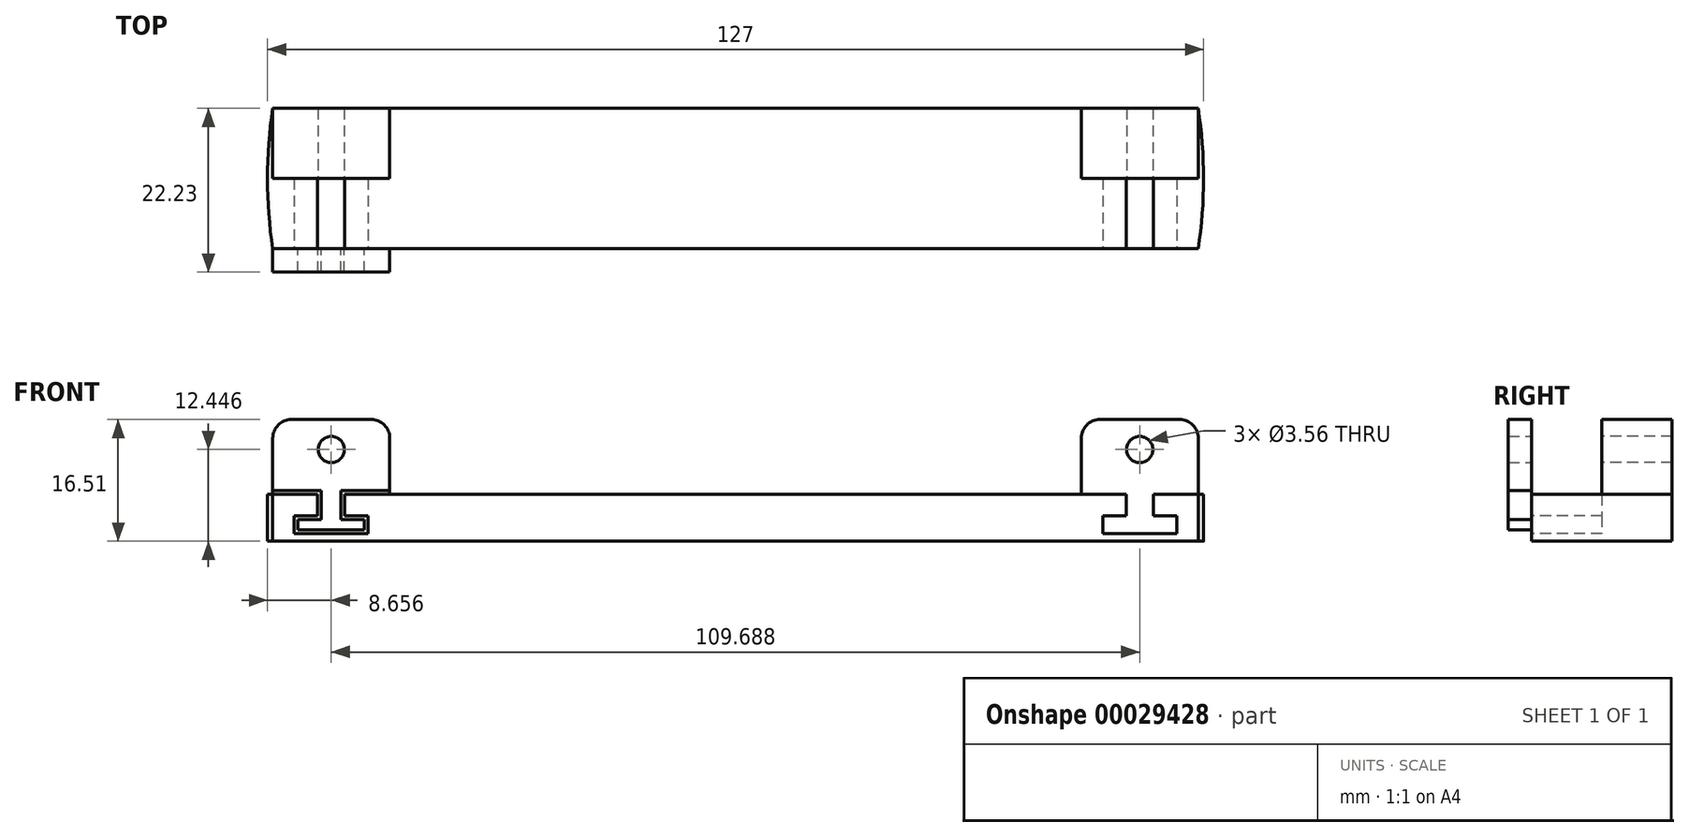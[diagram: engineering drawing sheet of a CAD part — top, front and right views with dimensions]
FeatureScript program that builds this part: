
annotation { "Feature Type Name" : "Feature", "Feature Type Description" : "" }
export const myFeature = defineFeature(function(context is Context, id is Id, definition is map)
    precondition{}
    {
        {
            var Q0;
            Q0=qCreatedBy(makeId("Top.planeOp"),FACE);
            var sketch = newSketch(context, id + "F0", { "sketchPlane" : qUnion([Q0])});
            skArc(sketch, "E0", {"start": v(-62.78, 9.52) * mm, "mid": v(-63.5, 0) * mm, "end": v(-62.78, -9.53) * mm});
            skLineSegment(sketch, "E1", {"start": v(0, 9.53) * mm, "end": v(-62.78, 9.53) * mm});
            skLineSegment(sketch, "E2", {"start": v(0, 9.53) * mm, "end": v(62.78, 9.53) * mm});
            skLineSegment(sketch, "E3", {"start": v(0, -9.53) * mm, "end": v(62.78, -9.53) * mm});
            skLineSegment(sketch, "E4", {"start": v(0, -9.53) * mm, "end": v(-62.78, -9.53) * mm});
            skArc(sketch, "E5.trimOffspring", {"start": v(62.78, -9.52) * mm, "mid": v(63.5, 0) * mm, "end": v(62.78, 9.53) * mm});
            skSolve(sketch);
        }
        {
            var Q0;
            Q0 = qSketchRegion(id + "F0", true);
            extrude(context, id + "F1", {"entities" : qUnion([Q0]), "depth" : 6.35 * mm});
        }
        {
            var Q0;
            Q0=makeQuery(id+"F1.opExtrude","SWEPT_FACE",FACE,{"disambiguationData":[OSD([sQuery(id+"F0.wireOp",EDGE,"E3"),sQuery(id+"F0.wireOp",EDGE,"E4")])]});
            var sketch = newSketch(context, id + "F2", { "sketchPlane" : qUnion([Q0])});
            skLineSegment(sketch, "E6", {"start": v(0, 0) * mm, "end": v(0, 18.8) * mm});
            skLineSegment(sketch, "E7", {"start": v(-56.69, 6.35) * mm, "end": v(-56.69, 3.43) * mm});
            skLineSegment(sketch, "E8", {"start": v(-56.69, 3.43) * mm, "end": v(-59.86, 3.43) * mm});
            skLineSegment(sketch, "E9", {"start": v(-59.86, 3.43) * mm, "end": v(-59.86, 1.02) * mm});
            skLineSegment(sketch, "E10", {"start": v(-59.86, 1.02) * mm, "end": v(-49.83, 1.02) * mm});
            skLineSegment(sketch, "E11", {"start": v(-49.83, 1.02) * mm, "end": v(-49.83, 3.43) * mm});
            skLineSegment(sketch, "E12", {"start": v(-49.83, 3.43) * mm, "end": v(-53, 3.43) * mm});
            skLineSegment(sketch, "E13", {"start": v(-53, 3.43) * mm, "end": v(-53, 6.35) * mm});
            skLineSegment(sketch, "E14", {"start": v(-56.69, 6.35) * mm, "end": v(-53, 6.35) * mm});
            skLineSegment(sketch, "E15.MirrorCS", {"start": v(53, 3.43) * mm, "end": v(53, 6.35) * mm});
            skLineSegment(sketch, "E16.MirrorCS", {"start": v(56.69, 6.35) * mm, "end": v(53, 6.35) * mm});
            skLineSegment(sketch, "E17.MirrorCS", {"start": v(49.83, 3.43) * mm, "end": v(53, 3.43) * mm});
            skLineSegment(sketch, "E18.MirrorCS", {"start": v(56.69, 6.35) * mm, "end": v(56.69, 3.43) * mm});
            skLineSegment(sketch, "E19.MirrorCS", {"start": v(56.69, 3.43) * mm, "end": v(59.86, 3.43) * mm});
            skLineSegment(sketch, "E20.MirrorCS", {"start": v(59.86, 3.43) * mm, "end": v(59.86, 1.02) * mm});
            skLineSegment(sketch, "E21.MirrorCS", {"start": v(49.83, 1.02) * mm, "end": v(49.83, 3.43) * mm});
            skLineSegment(sketch, "E22.MirrorCS", {"start": v(59.86, 1.02) * mm, "end": v(49.83, 1.02) * mm});
            skSolve(sketch);
        }
        {
            var Q0;
            Q0 = qSketchRegion(id + "F2", true);
            extrude(context, id + "F3", {"entities" : qUnion([Q0]), "operationType" : NewBodyOperationType.REMOVE, "oppositeDirection" : true, "depth" : 25.4 * mm});
        }
        {
            var Q0;
            Q0=qCreatedBy(makeId("Front.planeOp"),FACE);
            var sketch = newSketch(context, id + "F4", { "sketchPlane" : qUnion([Q0])});
            skLineSegment(sketch, "E23.0", {"start": v(-62.78, 6.35) * mm, "end": v(-62.78, 0) * mm});
            skLineSegment(sketch, "E24", {"start": v(-62.78, 6.35) * mm, "end": v(-62.78, 13.97) * mm});
            skLineSegment(sketch, "E25.0", {"start": v(-53, 3.43) * mm, "end": v(-53, 6.35) * mm});
            skLineSegment(sketch, "E26.0", {"start": v(-56.69, 6.35) * mm, "end": v(-56.69, 3.43) * mm});
            skLineSegment(sketch, "E27", {"start": v(-46.9, 13.97) * mm, "end": v(-46.9, 6.35) * mm});
            skLineSegment(sketch, "E28", {"start": v(-46.9, 6.35) * mm, "end": v(-46.9, 0) * mm});
            skLineSegment(sketch, "E29", {"start": v(-46.9, 0) * mm, "end": v(-62.78, 0) * mm});
            skLineSegment(sketch, "E30", {"start": v(-60.24, 16.51) * mm, "end": v(-49.45, 16.51) * mm});
            skPoint(sketch, "E31.visualSharp", {"position": v(-62.78, 16.51) * mm});
            skArc(sketch, "E31.filletArc", {"start": v(-60.24, 16.51) * mm, "mid": v(-62.04, 15.77) * mm, "end": v(-62.78, 13.97) * mm});
            skPoint(sketch, "E32.visualSharp", {"position": v(-46.9, 16.51) * mm});
            skArc(sketch, "E32.filletArc", {"start": v(-46.9, 13.97) * mm, "mid": v(-47.65, 15.77) * mm, "end": v(-49.45, 16.51) * mm});
            skSolve(sketch);
        }
        {
            var Q0;
            Q0 = qSketchRegion(id + "F4", true);
            extrude(context, id + "F5", {"entities" : qUnion([Q0]), "operationType" : NewBodyOperationType.ADD, "oppositeDirection" : true, "depth" : 3.17 * mm});
        }
        {
            var Q0;
            Q0=makeQuery(id+"F5.opExtrude","CAP_FACE",FACE,{"disambiguationData":[OSD([sQuery(id+"F4.wireOp",EDGE,"E23.0"),sQuery(id+"F4.wireOp",EDGE,"E24"),sQuery(id+"F4.wireOp",EDGE,"E27"),sQuery(id+"F4.wireOp",EDGE,"E28"),sQuery(id+"F4.wireOp",EDGE,"E29"),sQuery(id+"F4.wireOp",EDGE,"E30"),sQuery(id+"F4.wireOp",EDGE,"E31.filletArc"),sQuery(id+"F4.wireOp",EDGE,"E32.filletArc")])],"isStart":true});
            var sketch = newSketch(context, id + "F6", { "sketchPlane" : qUnion([Q0])});
            skCircle(sketch, "E33", {"center": v(-54.84, 12.45) * mm, "radius": 1.78 * mm});
            skSolve(sketch);
        }
        {
            var Q0;
            Q0 = qSketchRegion(id + "F6", true);
            extrude(context, id + "F7", {"entities" : qUnion([Q0]), "operationType" : NewBodyOperationType.REMOVE, "oppositeDirection" : true, "depth" : 25.4 * mm});
        }
        {
            var Q0;
            Q0=makeQuery(id+"F1.opExtrude","SWEPT_BODY",BODY,{"disambiguationData":[OSD([sQuery(id+"F0.wireOp",EDGE,"E0"),sQuery(id+"F0.wireOp",EDGE,"E1"),sQuery(id+"F0.wireOp",EDGE,"E2"),sQuery(id+"F0.wireOp",EDGE,"E3"),sQuery(id+"F0.wireOp",EDGE,"E4"),sQuery(id+"F0.wireOp",EDGE,"E5.trimOffspring")])]});
            var Q1;
            Q1=qCreatedBy(makeId("Right.planeOp"),FACE);
            mirror(context, id + "F8", {"operationType" : NewBodyOperationType.ADD, "entities" : qUnion([Q0]), "mirrorPlane" : qUnion([Q1])});
        }
        {
            var Q0;
            Q0=makeQuery(id+"F1.opExtrude","SWEPT_FACE",FACE,{"disambiguationData":[OSD([sQuery(id+"F0.wireOp",EDGE,"E3"),sQuery(id+"F0.wireOp",EDGE,"E4")])]});
            var sketch = newSketch(context, id + "F9", { "sketchPlane" : qUnion([Q0])});
            skLineSegment(sketch, "E34", {"start": v(-56.18, 2.92) * mm, "end": v(-59.35, 2.92) * mm});
            skLineSegment(sketch, "E35", {"start": v(-59.35, 2.92) * mm, "end": v(-59.35, 1.52) * mm});
            skLineSegment(sketch, "E36", {"start": v(-59.35, 1.52) * mm, "end": v(-50.34, 1.52) * mm});
            skLineSegment(sketch, "E37", {"start": v(-50.34, 1.52) * mm, "end": v(-50.34, 2.92) * mm});
            skLineSegment(sketch, "E38", {"start": v(-50.34, 2.92) * mm, "end": v(-53.51, 2.92) * mm});
            skLineSegment(sketch, "E39", {"start": v(-53.51, 2.92) * mm, "end": v(-53.51, 6.86) * mm});
            skLineSegment(sketch, "E40", {"start": v(-56.18, 2.92) * mm, "end": v(-56.18, 6.86) * mm});
            skLineSegment(sketch, "E41.0", {"start": v(-62.78, 6.86) * mm, "end": v(-62.78, 13.97) * mm});
            skArc(sketch, "E42.0", {"start": v(-60.24, 16.51) * mm, "mid": v(-62.04, 15.77) * mm, "end": v(-62.78, 13.97) * mm});
            skLineSegment(sketch, "E43.0", {"start": v(-60.24, 16.51) * mm, "end": v(-49.45, 16.51) * mm});
            skArc(sketch, "E44.0", {"start": v(-46.9, 13.97) * mm, "mid": v(-47.65, 15.77) * mm, "end": v(-49.45, 16.51) * mm});
            skLineSegment(sketch, "E45.0", {"start": v(-46.9, 13.97) * mm, "end": v(-46.9, 6.86) * mm});
            skLineSegment(sketch, "E46", {"start": v(-56.18, 6.86) * mm, "end": v(-62.78, 6.86) * mm});
            skLineSegment(sketch, "E47", {"start": v(-53.51, 6.86) * mm, "end": v(-46.9, 6.86) * mm});
            skPoint(sketch, "E48.orphan", {"position": v(-62.78, 6.35) * mm});
            skPoint(sketch, "E49.orphan", {"position": v(-46.9, 6.35) * mm});
            skCircle(sketch, "E50.0", {"center": v(-54.84, 12.45) * mm, "radius": 1.78 * mm});
            skSolve(sketch);
        }
        {
            var Q0;
            Q0 = qSketchRegion(id + "F9", true);
            extrude(context, id + "F10", {"entities" : qUnion([Q0]), "depth" : 3.17 * mm});
        }
        {
            var Q0;
            Q0=makeQuery(id+"F8.opPattern","COPY",FACE,{"derivedFrom":makeQuery(id+"F5.opExtrude","CAP_FACE",FACE,{"disambiguationData":[OSD([sQuery(id+"F4.wireOp",EDGE,"E23.0"),sQuery(id+"F4.wireOp",EDGE,"E24"),sQuery(id+"F4.wireOp",EDGE,"E27"),sQuery(id+"F4.wireOp",EDGE,"E28"),sQuery(id+"F4.wireOp",EDGE,"E29"),sQuery(id+"F4.wireOp",EDGE,"E30"),sQuery(id+"F4.wireOp",EDGE,"E31.filletArc"),sQuery(id+"F4.wireOp",EDGE,"E32.filletArc")])],"isStart":false}),"instanceName":"1"});
            var sketch = newSketch(context, id + "F11", { "sketchPlane" : qUnion([Q0])});
            skLineSegment(sketch, "E51.0.0", {"start": v(-62.78, 6.35) * mm, "end": v(-56.69, 6.35) * mm});
            skLineSegment(sketch, "E51.0.1", {"start": v(-56.69, 6.35) * mm, "end": v(-56.69, 3.43) * mm});
            skLineSegment(sketch, "E51.0.2", {"start": v(-56.69, 3.43) * mm, "end": v(-59.86, 3.43) * mm});
            skLineSegment(sketch, "E51.0.3", {"start": v(-59.86, 3.43) * mm, "end": v(-59.86, 1.02) * mm});
            skLineSegment(sketch, "E51.0.4", {"start": v(-59.86, 1.02) * mm, "end": v(-49.83, 1.02) * mm});
            skLineSegment(sketch, "E51.0.5", {"start": v(-49.83, 1.02) * mm, "end": v(-49.83, 3.43) * mm});
            skLineSegment(sketch, "E51.0.6", {"start": v(-49.83, 3.43) * mm, "end": v(-53, 3.43) * mm});
            skLineSegment(sketch, "E51.0.7", {"start": v(-53, 3.43) * mm, "end": v(-53, 6.35) * mm});
            skLineSegment(sketch, "E51.0.8", {"start": v(-53, 6.35) * mm, "end": v(-46.9, 6.35) * mm});
            skLineSegment(sketch, "E51.0.9", {"start": v(-46.9, 6.35) * mm, "end": v(-46.9, 13.97) * mm});
            skArc(sketch, "E51.0.10", {"start": v(-46.9, 13.97) * mm, "mid": v(-47.65, 15.77) * mm, "end": v(-49.45, 16.51) * mm});
            skLineSegment(sketch, "E51.0.11", {"start": v(-49.45, 16.51) * mm, "end": v(-60.24, 16.51) * mm});
            skArc(sketch, "E51.0.12", {"start": v(-60.24, 16.51) * mm, "mid": v(-62.04, 15.77) * mm, "end": v(-62.78, 13.97) * mm});
            skLineSegment(sketch, "E51.0.13", {"start": v(-62.78, 13.97) * mm, "end": v(-62.78, 6.35) * mm});
            skCircle(sketch, "E52.0", {"center": v(-54.84, 12.45) * mm, "radius": 1.78 * mm});
            skLineSegment(sketch, "E53.0.0", {"start": v(56.69, 6.35) * mm, "end": v(62.78, 6.35) * mm});
            skLineSegment(sketch, "E53.0.1", {"start": v(62.78, 6.35) * mm, "end": v(62.78, 13.97) * mm});
            skArc(sketch, "E53.0.2", {"start": v(62.78, 13.97) * mm, "mid": v(62.04, 15.77) * mm, "end": v(60.24, 16.51) * mm});
            skLineSegment(sketch, "E53.0.3", {"start": v(60.24, 16.51) * mm, "end": v(49.45, 16.51) * mm});
            skArc(sketch, "E53.0.4", {"start": v(49.45, 16.51) * mm, "mid": v(47.65, 15.77) * mm, "end": v(46.9, 13.97) * mm});
            skLineSegment(sketch, "E53.0.5", {"start": v(46.9, 13.97) * mm, "end": v(46.9, 6.35) * mm});
            skLineSegment(sketch, "E53.0.6", {"start": v(46.9, 6.35) * mm, "end": v(53, 6.35) * mm});
            skLineSegment(sketch, "E53.0.7", {"start": v(53, 6.35) * mm, "end": v(53, 3.43) * mm});
            skLineSegment(sketch, "E53.0.8", {"start": v(53, 3.43) * mm, "end": v(49.83, 3.43) * mm});
            skLineSegment(sketch, "E53.0.9", {"start": v(49.83, 3.43) * mm, "end": v(49.83, 1.02) * mm});
            skLineSegment(sketch, "E53.0.10", {"start": v(49.83, 1.02) * mm, "end": v(59.86, 1.02) * mm});
            skLineSegment(sketch, "E53.0.11", {"start": v(59.86, 1.02) * mm, "end": v(59.86, 3.43) * mm});
            skLineSegment(sketch, "E53.0.12", {"start": v(59.86, 3.43) * mm, "end": v(56.69, 3.43) * mm});
            skLineSegment(sketch, "E53.0.13", {"start": v(56.69, 3.43) * mm, "end": v(56.69, 6.35) * mm});
            skCircle(sketch, "E54.0", {"center": v(54.84, 12.45) * mm, "radius": 1.78 * mm});
            skSolve(sketch);
        }
        {
            var Q0;
            Q0 = qSketchRegion(id + "F11", true);
            var Q1;
            Q1=makeQuery(id+"F1.opExtrude","SWEPT_FACE",FACE,{"disambiguationData":[OSD([sQuery(id+"F0.wireOp",EDGE,"E1"),sQuery(id+"F0.wireOp",EDGE,"E2")])]});
            extrude(context, id + "F12", {"entities" : qUnion([Q0]), "operationType" : NewBodyOperationType.ADD, "endBound" : BoundingType.UP_TO_SURFACE, "endBoundEntityFace" : qUnion([Q1]), "depth" : 25.4 * mm});
        }
    });
